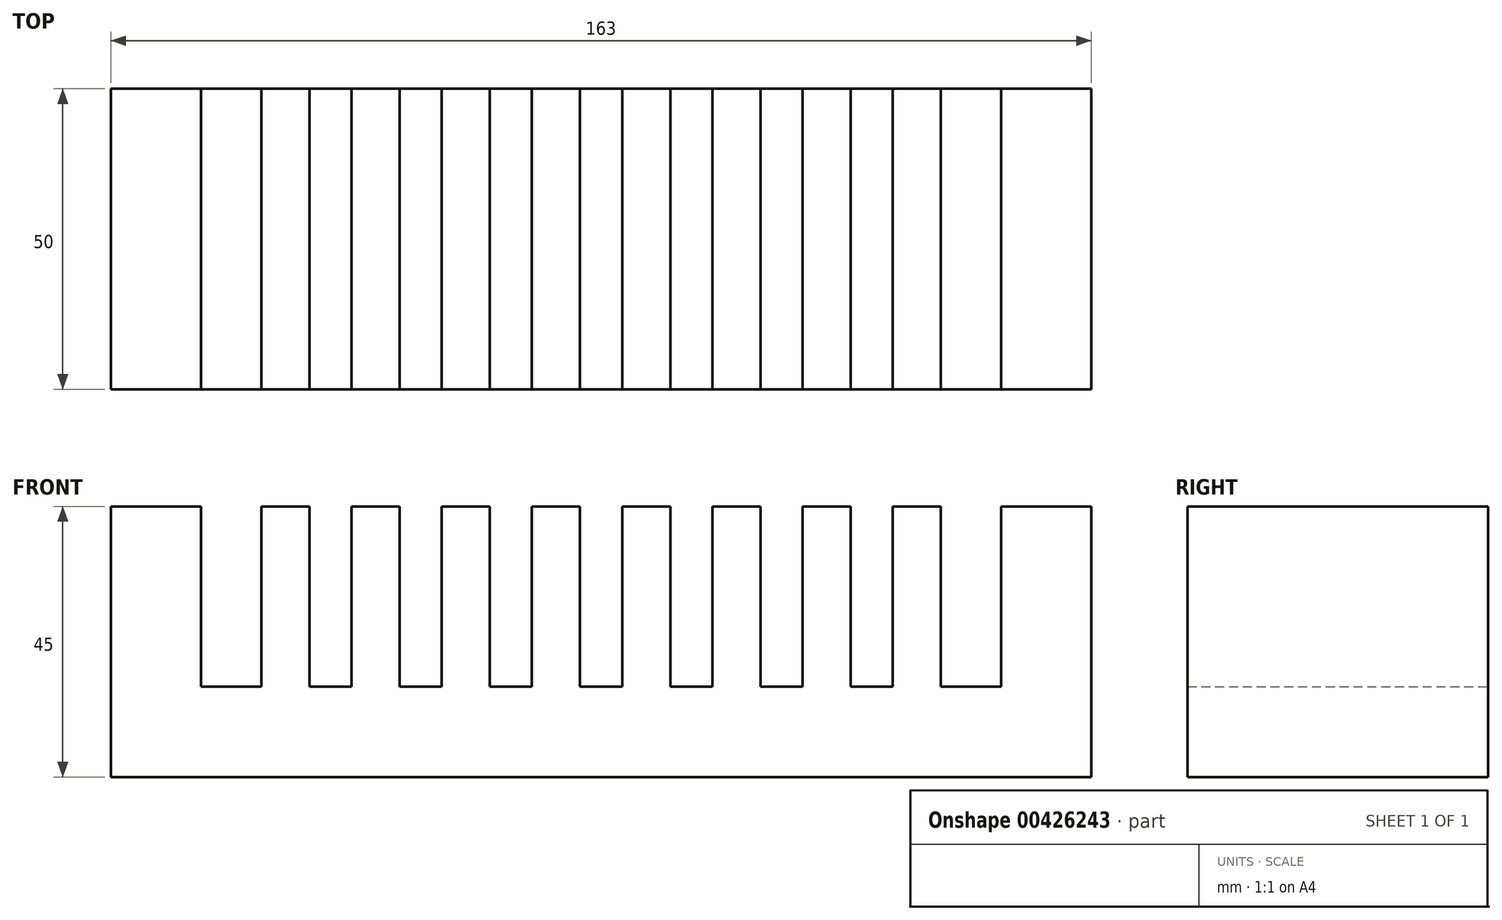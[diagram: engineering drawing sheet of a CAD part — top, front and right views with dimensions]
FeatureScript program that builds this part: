
annotation { "Feature Type Name" : "Feature", "Feature Type Description" : "" }
export const myFeature = defineFeature(function(context is Context, id is Id, definition is map)
    precondition{}
    {
        {
            var Q0;
            Q0=qCreatedBy(makeId("Front.planeOp"),FACE);
            var sketch = newSketch(context, id + "F0", { "sketchPlane" : qUnion([Q0])});
            skLineSegment(sketch, "E0.bottom", {"start": v(81.5, -22.5) * mm, "end": v(-81.5, -22.5) * mm});
            skLineSegment(sketch, "E0.top", {"start": v(81.5, 22.5) * mm, "end": v(66.5, 22.5) * mm});
            skLineSegment(sketch, "E0.left", {"start": v(81.5, -22.5) * mm, "end": v(81.5, 22.5) * mm});
            skLineSegment(sketch, "E0.right", {"start": v(-81.5, -22.5) * mm, "end": v(-81.5, 22.5) * mm});
            skPoint(sketch, "E0.middle", {"position": v(0, 0) * mm});
            skLineSegment(sketch, "E1", {"start": v(-66.5, -7.5) * mm, "end": v(-56.5, -7.5) * mm});
            skLineSegment(sketch, "E2", {"start": v(-3.5, 22.5) * mm, "end": v(-3.5, -7.5) * mm});
            skLineSegment(sketch, "E3.MirrorCS", {"start": v(3.5, 22.5) * mm, "end": v(3.5, -7.5) * mm});
            skLineSegment(sketch, "E4", {"start": v(11.5, 22.5) * mm, "end": v(11.5, -7.5) * mm});
            skLineSegment(sketch, "E5", {"start": v(18.5, 22.5) * mm, "end": v(18.5, -7.5) * mm});
            skLineSegment(sketch, "E6", {"start": v(26.5, 22.5) * mm, "end": v(26.5, -7.5) * mm});
            skLineSegment(sketch, "E7", {"start": v(33.5, 22.5) * mm, "end": v(33.5, -7.5) * mm});
            skLineSegment(sketch, "E8", {"start": v(41.5, 22.5) * mm, "end": v(41.5, -7.5) * mm});
            skLineSegment(sketch, "E9", {"start": v(48.5, 22.5) * mm, "end": v(48.5, -7.5) * mm});
            skLineSegment(sketch, "E10", {"start": v(56.5, 22.5) * mm, "end": v(56.5, -7.5) * mm});
            skLineSegment(sketch, "E11", {"start": v(66.5, 22.5) * mm, "end": v(66.5, -7.5) * mm});
            skLineSegment(sketch, "E12.MirrorCS", {"start": v(-11.5, 22.5) * mm, "end": v(-11.5, -7.5) * mm});
            skLineSegment(sketch, "E13.MirrorCS", {"start": v(-18.5, 22.5) * mm, "end": v(-18.5, -7.5) * mm});
            skLineSegment(sketch, "E14.MirrorCS", {"start": v(-26.5, 22.5) * mm, "end": v(-26.5, -7.5) * mm});
            skLineSegment(sketch, "E15.MirrorCS", {"start": v(-33.5, 22.5) * mm, "end": v(-33.5, -7.5) * mm});
            skLineSegment(sketch, "E16.MirrorCS", {"start": v(-41.5, 22.5) * mm, "end": v(-41.5, -7.5) * mm});
            skLineSegment(sketch, "E17.MirrorCS", {"start": v(-48.5, 22.5) * mm, "end": v(-48.5, -7.5) * mm});
            skLineSegment(sketch, "E18.MirrorCS", {"start": v(-56.5, 22.5) * mm, "end": v(-56.5, -7.5) * mm});
            skLineSegment(sketch, "E19.MirrorCS", {"start": v(-66.5, 22.5) * mm, "end": v(-66.5, -7.5) * mm});
            skLineSegment(sketch, "E20.trimOffspring", {"start": v(56.5, 22.5) * mm, "end": v(48.5, 22.5) * mm});
            skLineSegment(sketch, "E21.trimOffspring", {"start": v(41.5, 22.5) * mm, "end": v(33.5, 22.5) * mm});
            skLineSegment(sketch, "E22.trimOffspring", {"start": v(26.5, 22.5) * mm, "end": v(18.5, 22.5) * mm});
            skLineSegment(sketch, "E23.trimOffspring", {"start": v(11.5, 22.5) * mm, "end": v(3.5, 22.5) * mm});
            skLineSegment(sketch, "E24.trimOffspring", {"start": v(-3.5, 22.5) * mm, "end": v(-11.5, 22.5) * mm});
            skLineSegment(sketch, "E25.trimOffspring", {"start": v(-18.5, 22.5) * mm, "end": v(-26.5, 22.5) * mm});
            skLineSegment(sketch, "E26.trimOffspring", {"start": v(-33.5, 22.5) * mm, "end": v(-41.5, 22.5) * mm});
            skLineSegment(sketch, "E27.trimOffspring", {"start": v(-48.5, 22.5) * mm, "end": v(-56.5, 22.5) * mm});
            skLineSegment(sketch, "E28.trimOffspring", {"start": v(-66.5, 22.5) * mm, "end": v(-81.5, 22.5) * mm});
            skLineSegment(sketch, "E29.trimOffspring", {"start": v(-48.5, -7.5) * mm, "end": v(-41.5, -7.5) * mm});
            skLineSegment(sketch, "E30.trimOffspring", {"start": v(-33.5, -7.5) * mm, "end": v(-26.5, -7.5) * mm});
            skLineSegment(sketch, "E31.trimOffspring", {"start": v(-18.5, -7.5) * mm, "end": v(-11.5, -7.5) * mm});
            skLineSegment(sketch, "E32.trimOffspring", {"start": v(-3.5, -7.5) * mm, "end": v(3.5, -7.5) * mm});
            skLineSegment(sketch, "E33.trimOffspring", {"start": v(11.5, -7.5) * mm, "end": v(18.5, -7.5) * mm});
            skLineSegment(sketch, "E34.trimOffspring", {"start": v(26.5, -7.5) * mm, "end": v(33.5, -7.5) * mm});
            skLineSegment(sketch, "E35.trimOffspring", {"start": v(41.5, -7.5) * mm, "end": v(48.5, -7.5) * mm});
            skLineSegment(sketch, "E36.trimOffspring", {"start": v(56.5, -7.5) * mm, "end": v(66.5, -7.5) * mm});
            skSolve(sketch);
        }
        {
            var Q0;
            Q0 = qSketchRegion(id + "F0", true);
            extrude(context, id + "F1", {"entities" : qUnion([Q0]), "depth" : 50 * mm});
        }
    });
